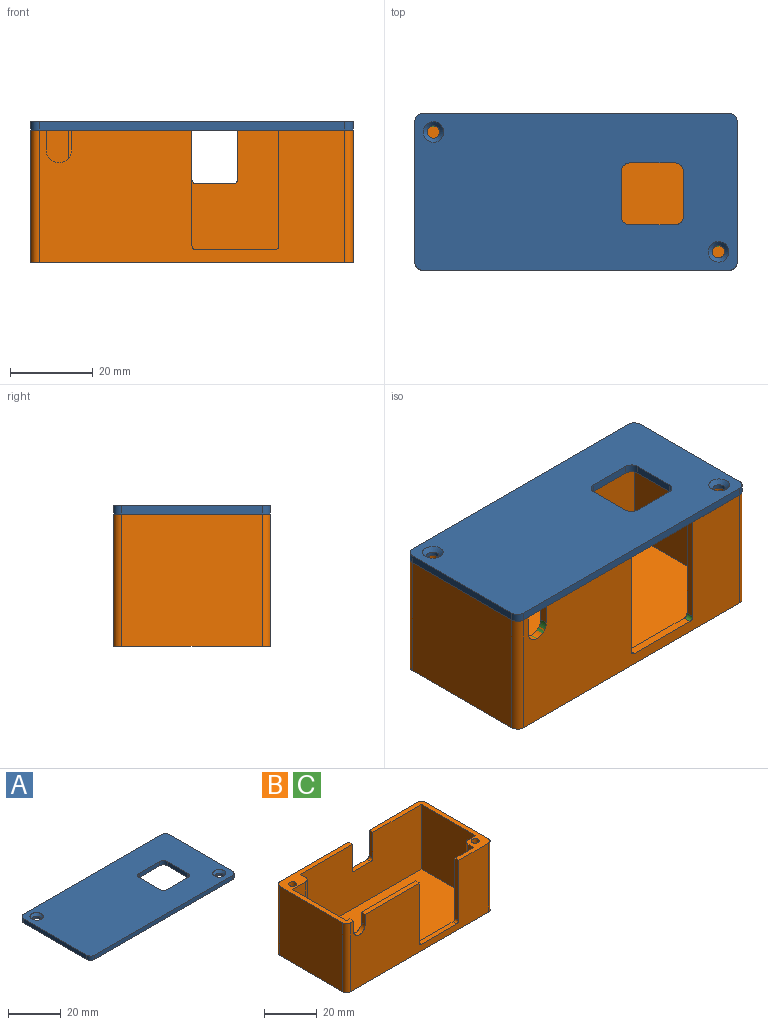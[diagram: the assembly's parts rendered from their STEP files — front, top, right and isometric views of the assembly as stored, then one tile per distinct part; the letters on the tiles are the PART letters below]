
ASSEMBLY  parts=3 mates=1
PART A: 22 faces, bbox 78x38x2 mm
  f0: plane 78x38mm, normal (0,0,1), area 2699.7mm2, adj f2,f3,f4,f5,f6,f7,f8,f9
  f1: plane 78x38mm, normal (0,0,-1), area 2724.9mm2, adj f2,f3,f4,f5,f6,f7,f8,f9
  f2: plane 34x2mm, normal (-1,0,0), area 68mm2, adj f0,f1,f6,f9
  f3: plane 74x2mm, normal (0,-1,0), area 148mm2, adj f0,f1,f6,f7
  f4: plane 34x2mm, normal (1,0,0), area 68mm2, adj f0,f1,f7,f8
  f5: plane 74x2mm, normal (0,1,0), area 148mm2, adj f0,f1,f8,f9
  f6: cylinder r=2mm len=2mm, axis (0,0,1), area 6.3mm2, adj f0,f1,f2,f3
  f7: cylinder r=2mm len=2mm, axis (0,0,-1), area 6.3mm2, adj f0,f1,f3,f4
  f8: cylinder r=2mm len=2mm, axis (0,0,1), area 6.3mm2, adj f0,f1,f4,f5
  f9: cylinder r=2mm len=2mm, axis (0,0,-1), area 6.3mm2, adj f0,f1,f2,f5
  f10: cylinder r=1.5mm len=3mm, axis (0,0,1), area 9.4mm2, adj f1,f12
  f11: cylinder r=1.5mm len=3mm, axis (0,0,1), area 9.4mm2, adj f1,f13
  f12: cone r=1.5mm half-angle=45deg, axis (0,0,1), area 17.8mm2, adj f0,f10
  f13: cone r=1.5mm half-angle=45deg, axis (0,0,1), area 17.8mm2, adj f0,f11
  f14: plane 11x2mm, normal (0,-1,0), area 22mm2, adj f0,f1,f18,f21
  f15: plane 11x2mm, normal (1,0,0), area 22mm2, adj f0,f1,f18,f19
  f16: plane 11x2mm, normal (0,1,0), area 22mm2, adj f0,f1,f19,f20
  f17: plane 11x2mm, normal (-1,0,0), area 22mm2, adj f0,f1,f20,f21
  f18: cylinder r=2mm len=2mm, axis (0,0,1), area 6.3mm2, adj f0,f1,f14,f15
  f19: cylinder r=2mm len=2mm, axis (0,0,-1), area 6.3mm2, adj f0,f1,f15,f16
  f20: cylinder r=2mm len=2mm, axis (0,0,1), area 6.3mm2, adj f0,f1,f16,f17
  f21: cylinder r=2mm len=2mm, axis (0,0,-1), area 6.3mm2, adj f0,f1,f14,f17
PART B: 44 faces, bbox 78x38x32 mm
  f0: plane 39x38mm, normal (0,0,1), area 188.8mm2, adj f1,f3,f5,f8,f10,f12,f13,f16
  f1: plane 65x30mm, normal (0,-1,0), area 1807.4mm2, adj f0,f2,f4,f7,f26,f33,f34,f35
  f2: plane 38x28mm, normal (0,0,1), area 180.4mm2, adj f1,f3,f5,f7,f9,f10,f14,f15
  f3: plane 74x32mm, normal (0,-1,0), area 1714.6mm2, adj f0,f2,f6,f11,f13,f14,f23,f24
  f4: plane 74x34mm, normal (0,0,1), area 2442.7mm2, adj f1,f5,f7,f12,f17,f18,f26,f27
  f5: plane 68x30mm, normal (0,1,0), area 1386.6mm2, adj f0,f2,f4,f6,f12,f23,f24,f25
  f6: plane 29.1x2mm, normal (0,0,1), area 58.2mm2, adj f3,f5,f24,f30
  f7: plane 30x29mm, normal (-1,0,0), area 870mm2, adj f1,f2,f4,f18
  f8: plane 34x32mm, normal (-1,0,0), area 1088mm2, adj f0,f11,f13,f16
  f9: plane 34x32mm, normal (1,0,0), area 1088mm2, adj f2,f11,f14,f15
  f10: plane 74x32mm, normal (0,1,0), area 2225.4mm2, adj f0,f2,f11,f15,f16,f33,f34,f35
  f11: plane 78x38mm, normal (0,0,-1), area 2946.4mm2, adj f3,f8,f9,f10,f13,f14,f15,f16
  f12: plane 30x29mm, normal (1,0,0), area 870mm2, adj f0,f4,f5,f17
  f13: cylinder r=2mm len=32mm, axis (0,0,1), area 100.5mm2, adj f0,f3,f8,f11
  f14: cylinder r=2mm len=32mm, axis (0,0,-1), area 100.5mm2, adj f2,f3,f9,f11
  f15: cylinder r=2mm len=32mm, axis (0,0,1), area 100.5mm2, adj f2,f9,f10,f11
  f16: cylinder r=2mm len=32mm, axis (0,0,-1), area 100.5mm2, adj f0,f8,f10,f11
  f17: plane 30x7mm, normal (0,-1,0), area 210mm2, adj f0,f4,f12,f29
  f18: plane 30x4mm, normal (0,1,0), area 120mm2, adj f2,f4,f7,f28
  f19: cylinder r=1.5mm len=10mm, axis (0,0,1), area 94.2mm2, adj f2,f20
  f20: plane 3x3mm, normal (0,0,1), area 7.1mm2, adj f19
  f21: cylinder r=1.5mm len=10mm, axis (0,0,1), area 94.2mm2, adj f0,f22
  f22: plane 3x3mm, normal (0,0,1), area 7.1mm2, adj f21
  f23: cylinder r=3.1mm len=6.2mm, axis (0,-1,0), area 19.5mm2, adj f3,f5,f24,f25
  f24: plane 4.8x2mm, normal (-1,0,0), area 9.6mm2, adj f3,f5,f6,f23
  f25: plane 4.8x2mm, normal (1,0,0), area 9.6mm2, adj f0,f3,f5,f23
  f26: plane 30x3mm, normal (1,0,0), area 90mm2, adj f0,f1,f4,f29
  f27: plane 30x3mm, normal (-1,0,0), area 90mm2, adj f2,f4,f5,f28
  f28: cylinder r=2mm len=30mm, axis (0,0,1), area 94.2mm2, adj f2,f4,f18,f27
  f29: cylinder r=2mm len=30mm, axis (0,0,1), area 94.2mm2, adj f0,f4,f17,f26
  f30: plane 28x2mm, normal (1,0,0), area 56mm2, adj f3,f5,f6,f38
  f31: plane 19x2mm, normal (0,0,1), area 38mm2, adj f3,f5,f38,f39
  f32: plane 28x2mm, normal (-1,0,0), area 56mm2, adj f2,f3,f5,f39
  f33: plane 12x2mm, normal (-1,0,0), area 24mm2, adj f1,f2,f10,f36
  f34: plane 9x2mm, normal (0,0,1), area 18mm2, adj f1,f10,f36,f37
  f35: plane 12x2mm, normal (1,0,0), area 24mm2, adj f0,f1,f10,f37
  f36: cylinder r=1mm len=2mm, axis (0,-1,0), area 3.1mm2, adj f1,f10,f33,f34
  f37: cylinder r=1mm len=2mm, axis (0,1,0), area 3.1mm2, adj f1,f10,f34,f35
  f38: cylinder r=1mm len=2mm, axis (0,1,0), area 3.1mm2, adj f3,f5,f30,f31
  f39: cylinder r=1mm len=2mm, axis (0,-1,0), area 3.1mm2, adj f3,f5,f31,f32
  f40: cylinder r=1.5mm len=10mm, axis (0,0,-1), area 94.2mm2, adj f11,f41
  f41: plane 3x3mm, normal (0,0,-1), area 7.1mm2, adj f40
  f42: cylinder r=1.5mm len=10mm, axis (0,0,-1), area 94.2mm2, adj f11,f43
  f43: plane 3x3mm, normal (0,0,-1), area 7.1mm2, adj f42
PART C: same geometry as B
PLACE A t=(7.3,-70.74,32)mm
PLACE B at identity fixed
PLACE C at identity
MATE slider B.f19 <-> A.f10  axis (0,0,1) through (34.5,-14.5,32)mm
